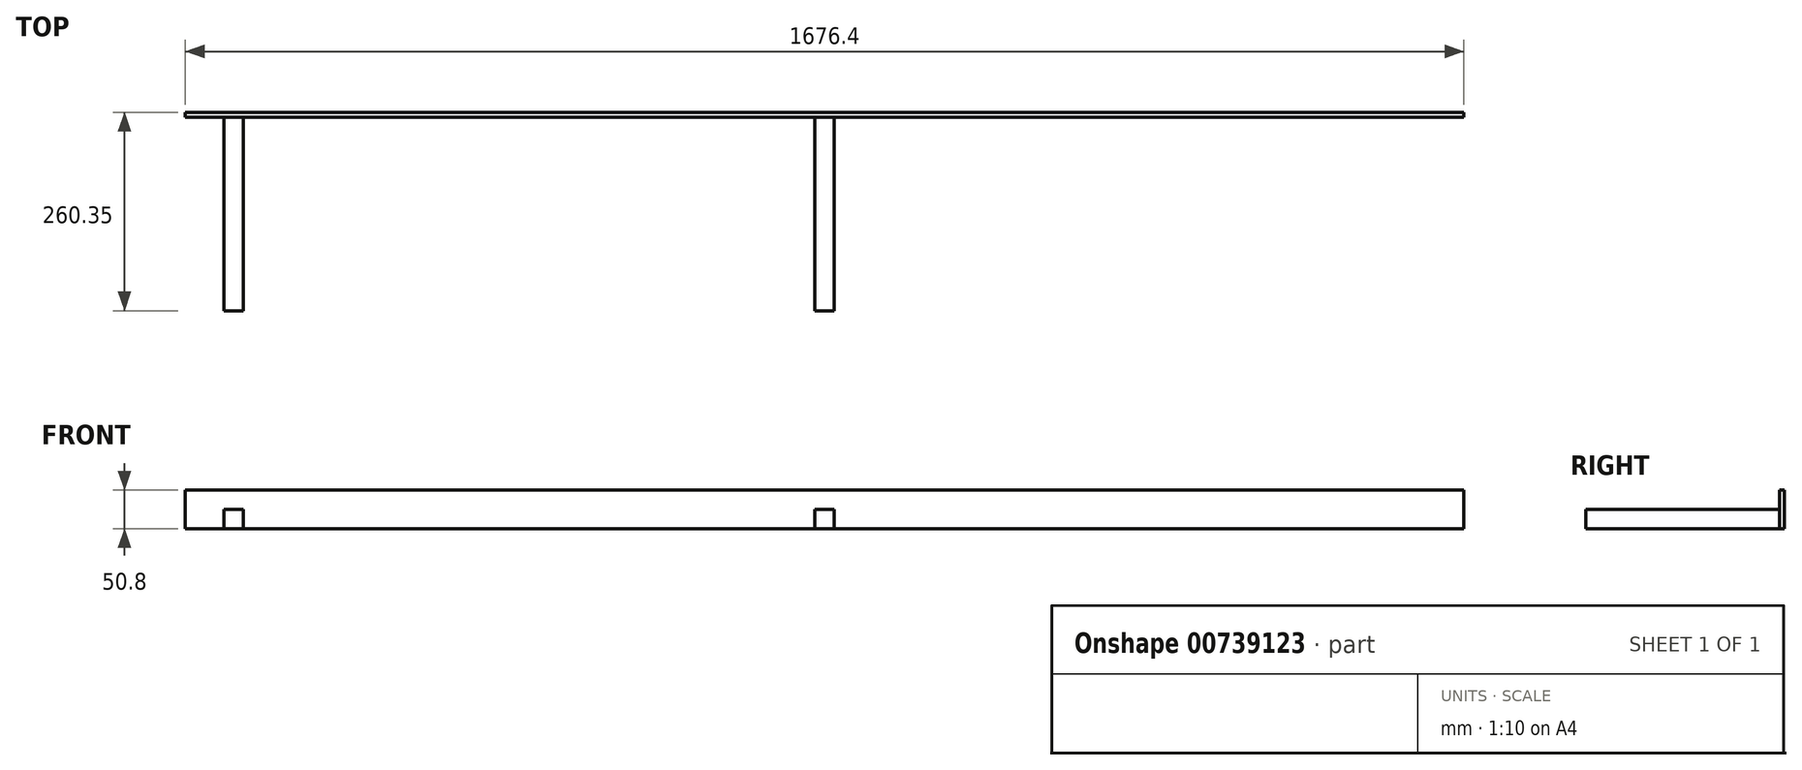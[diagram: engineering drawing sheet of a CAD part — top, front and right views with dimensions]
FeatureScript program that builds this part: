
annotation { "Feature Type Name" : "Feature", "Feature Type Description" : "" }
export const myFeature = defineFeature(function(context is Context, id is Id, definition is map)
    precondition{}
    {
        {
            var Q0;
            Q0=qCreatedBy(makeId("Front.planeOp"),FACE);
            var sketch = newSketch(context, id + "F0", { "sketchPlane" : qUnion([Q0])});
            skLineSegment(sketch, "E0.bottom", {"start": v(-838.2, 25.4) * mm, "end": v(838.2, 25.4) * mm});
            skLineSegment(sketch, "E0.top", {"start": v(-838.2, -25.4) * mm, "end": v(838.2, -25.4) * mm});
            skLineSegment(sketch, "E0.left", {"start": v(-838.2, 25.4) * mm, "end": v(-838.2, -25.4) * mm});
            skLineSegment(sketch, "E0.right", {"start": v(838.2, 25.4) * mm, "end": v(838.2, -25.4) * mm});
            skPoint(sketch, "E0.middle", {"position": v(0, 0) * mm});
            skSolve(sketch);
        }
        {
            var Q0;
            Q0=makeQuery(id+"F0.imprint","IMPRINT",FACE,{"disambiguationData":[TD([[makeQuery(id+"F0.imprint","IMPRINT",EDGE,{"derivedFrom":sQuery(id+"F0.wireOp",EDGE,"E0.bottom")}),-1.0]])]});
            extrude(context, id + "F1", {"entities" : qUnion([Q0]), "depth" : 6.35 * mm, "offsetDistance" : 25.4 * mm});
        }
        {
            var Q0;
            Q0=makeQuery(id+"F1.opExtrude","CAP_FACE",FACE,{"disambiguationData":[OSD([sQuery(id+"F0.wireOp",EDGE,"E0.bottom"),sQuery(id+"F0.wireOp",EDGE,"E0.top"),sQuery(id+"F0.wireOp",EDGE,"E0.left"),sQuery(id+"F0.wireOp",EDGE,"E0.right")])],"isStart":false});
            var sketch = newSketch(context, id + "F2", { "sketchPlane" : qUnion([Q0])});
            skLineSegment(sketch, "E1", {"start": v(0, 0) * mm, "end": v(-787.4, 0) * mm, "construction": true});
            skLineSegment(sketch, "E2.bottom", {"start": v(-787.4, 0) * mm, "end": v(-762, 0) * mm});
            skLineSegment(sketch, "E2.top", {"start": v(-787.4, -25.4) * mm, "end": v(-762, -25.4) * mm});
            skLineSegment(sketch, "E2.left", {"start": v(-787.4, 0) * mm, "end": v(-787.4, -25.4) * mm});
            skLineSegment(sketch, "E2.right", {"start": v(-762, 0) * mm, "end": v(-762, -25.4) * mm});
            skLineSegment(sketch, "E3.bottom", {"start": v(0, 0) * mm, "end": v(-12.7, 0) * mm});
            skLineSegment(sketch, "E3.top", {"start": v(0, -25.4) * mm, "end": v(-12.7, -25.4) * mm});
            skLineSegment(sketch, "E3.right", {"start": v(-12.7, 0) * mm, "end": v(-12.7, -25.4) * mm});
            skLineSegment(sketch, "E4.bottom", {"start": v(0, 0) * mm, "end": v(12.7, 0) * mm});
            skLineSegment(sketch, "E4.top", {"start": v(0, -25.4) * mm, "end": v(12.7, -25.4) * mm});
            skLineSegment(sketch, "E4.right", {"start": v(12.7, 0) * mm, "end": v(12.7, -25.4) * mm});
            skLineSegment(sketch, "E5", {"start": v(0, 0) * mm, "end": v(787.4, 0) * mm});
            skLineSegment(sketch, "E6.bottom", {"start": v(787.4, 0) * mm, "end": v(762, 0) * mm});
            skLineSegment(sketch, "E6.top", {"start": v(787.4, -25.4) * mm, "end": v(762, -25.4) * mm});
            skLineSegment(sketch, "E6.left", {"start": v(787.4, 0) * mm, "end": v(787.4, -25.4) * mm});
            skLineSegment(sketch, "E6.right", {"start": v(762, 0) * mm, "end": v(762, -25.4) * mm});
            skSolve(sketch);
        }
        {
            var Q0;
            Q0=makeQuery(id+"F2.imprint","IMPRINT",FACE,{"disambiguationData":[TD([[makeQuery(id+"F2.imprint","IMPRINT",EDGE,{"derivedFrom":sQuery(id+"F2.wireOp",EDGE,"E2.bottom")}),-1.0]])]});
            var Q1;
            Q1=makeQuery(id+"F2.imprint","IMPRINT",FACE,{"disambiguationData":[TD([[makeQuery(id+"F2.imprint","IMPRINT",EDGE,{"derivedFrom":sQuery(id+"F2.wireOp",EDGE,"E6.bottom")}),1.0]])]});
            var Q2;
            {var subQ0=sQuery(id+"F2.wireOp",EDGE,"E3.bottom");Q2=makeQuery(id+"F2.imprint","IMPRINT",FACE,{"disambiguationData":[TD([[makeQuery(id+"F2.imprint","IMPRINT",EDGE,{"derivedFrom":subQ0}),1.0]])]});}
            extrude(context, id + "F3", {"entities" : qUnion([Q0, Q1, Q2]), "operationType" : NewBodyOperationType.ADD, "depth" : 254 * mm, "offsetDistance" : 25.4 * mm});
        }
    });
